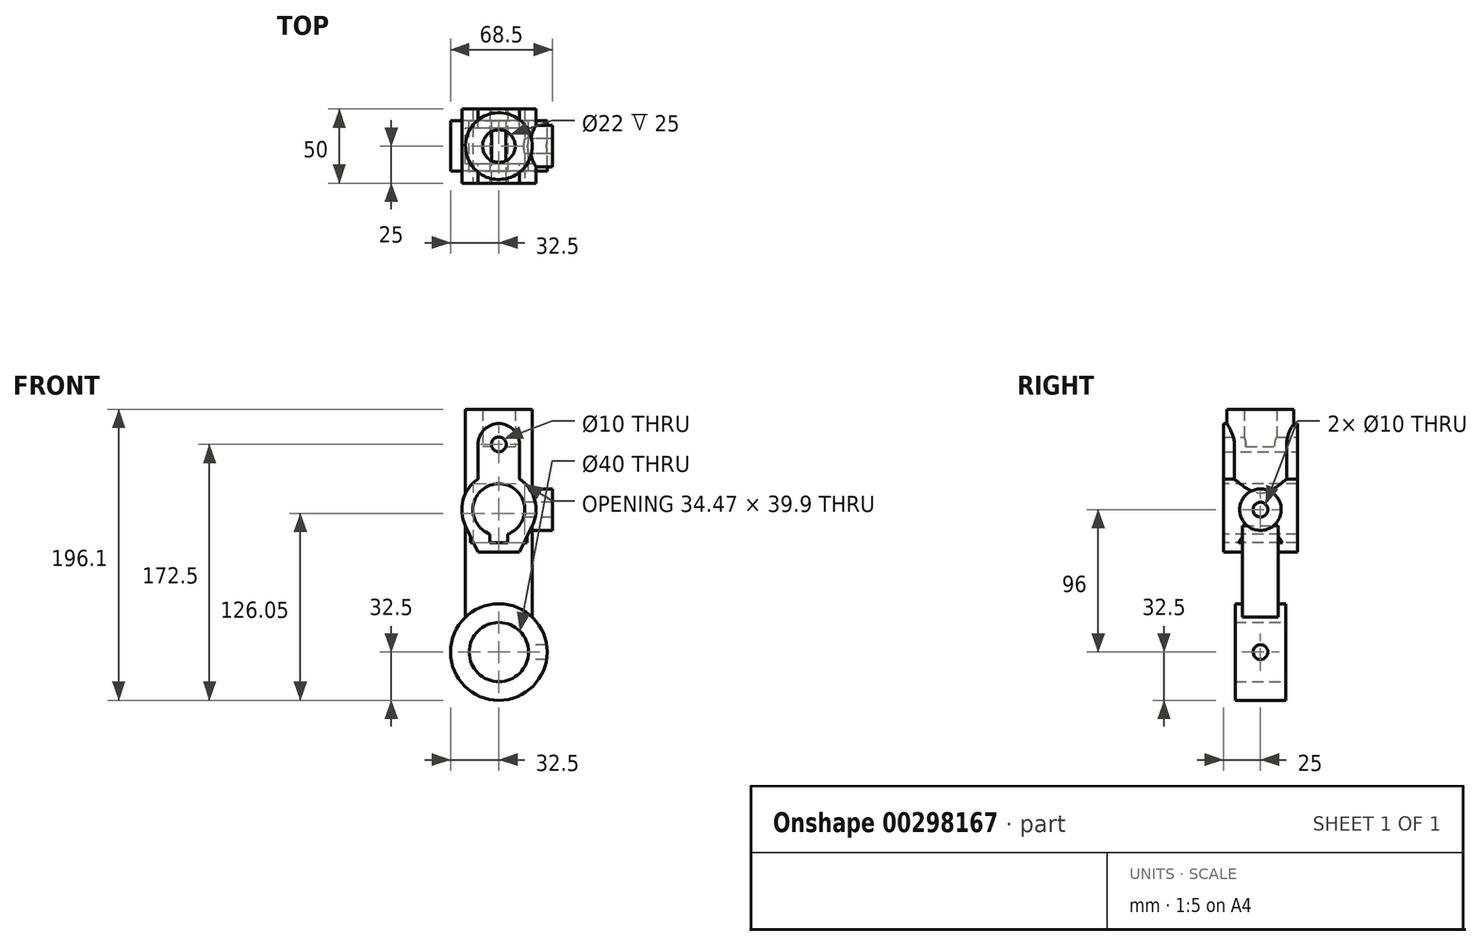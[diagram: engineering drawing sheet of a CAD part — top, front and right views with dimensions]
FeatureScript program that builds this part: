
annotation { "Feature Type Name" : "Feature", "Feature Type Description" : "" }
export const myFeature = defineFeature(function(context is Context, id is Id, definition is map)
    precondition{}
    {
        {
            var Q0;
            Q0=qCreatedBy(makeId("Front.planeOp"),FACE);
            var sketch = newSketch(context, id + "F0", { "sketchPlane" : qUnion([Q0])});
            skCircle(sketch, "E0", {"center": v(0, 0) * mm, "radius": 20 * mm});
            skCircle(sketch, "E1", {"center": v(0, 0) * mm, "radius": 32.5 * mm});
            skSolve(sketch);
        }
        {
            var Q0;
            Q0 = qSketchRegion(id + "F0", true);
            extrude(context, id + "F1", {"entities" : qUnion([Q0]), "endBound" : BoundingType.SYMMETRIC, "depth" : 34 * mm});
        }
        {
            var Q0;
            Q0=qCreatedBy(makeId("Right.planeOp"),FACE);
            var sketch = newSketch(context, id + "F2", { "sketchPlane" : qUnion([Q0])});
            skCircle(sketch, "E2", {"center": v(0, 0) * mm, "radius": 5 * mm});
            skSolve(sketch);
        }
        {
            var Q0;
            Q0 = qSketchRegion(id + "F2", true);
            extrude(context, id + "F3", {"entities" : qUnion([Q0]), "operationType" : NewBodyOperationType.REMOVE, "depth" : 100 * mm});
        }
        {
            var Q0;
            Q0=qCreatedBy(makeId("Front.planeOp"),FACE);
            var sketch = newSketch(context, id + "F4", { "sketchPlane" : qUnion([Q0])});
            skLineSegment(sketch, "E3.bottom", {"start": v(-22.5, 0) * mm, "end": v(22.5, 0) * mm});
            skLineSegment(sketch, "E3.top", {"start": v(-22.5, 96) * mm, "end": v(22.5, 96) * mm});
            skLineSegment(sketch, "E3.left", {"start": v(-22.5, 0) * mm, "end": v(-22.5, 96) * mm});
            skLineSegment(sketch, "E3.right", {"start": v(22.5, 0) * mm, "end": v(22.5, 96) * mm});
            skSolve(sketch);
        }
        {
            var Q0;
            Q0 = qSketchRegion(id + "F4", true);
            var Q1;
            Q1=makeQuery(id+"F1.opExtrude","SWEPT_FACE",FACE,{"disambiguationData":[OSD([sQuery(id+"F0.wireOp",EDGE,"E1")])]});
            var Q2;
            Q2=makeQuery(id+"F1.opExtrude","SWEPT_BODY",BODY,{"disambiguationData":[OSD([sQuery(id+"F0.wireOp",EDGE,"E0"),sQuery(id+"F0.wireOp",EDGE,"E1")])]});
            extrude(context, id + "F5", {"entities" : qUnion([Q0]), "operationType" : NewBodyOperationType.ADD, "endBound" : BoundingType.SYMMETRIC, "oppositeDirection" : true, "endBoundEntityFace" : qUnion([Q1]), "endBoundEntityBody" : qUnion([Q2]), "depth" : 24 * mm});
        }
        {
            var Q0;
            Q0=makeQuery(id+"F5.boolean.opBoolean","SPLIT",FACE,{"disambiguationData":[TD([makeQuery(id+"F3.boolean.opBoolean","COPY",FACE,{"derivedFrom":makeQuery(id+"F3.opExtrude","SWEPT_FACE",FACE,{"disambiguationData":[OSD([sQuery(id+"F2.wireOp",EDGE,"E2")])]})})])],"derivedFrom":makeQuery(id+"F5.opExtrude","SWEPT_FACE",FACE,{"disambiguationData":[OSD([sQuery(id+"F4.wireOp",EDGE,"E3.right")])]})});
            extrude(context, id + "F6", {"entities" : qUnion([Q0]), "operationType" : NewBodyOperationType.REMOVE, "oppositeDirection" : true, "depth" : 25 * mm});
        }
        {
            var Q0;
            {var subQ0=sQuery(id+"F4.wireOp",EDGE,"E3.bottom");Q0=makeQuery(id+"F5.boolean.opBoolean","SPLIT",FACE,{"disambiguationData":[TD([makeQuery(id+"F1.opExtrude","SWEPT_FACE",FACE,{"disambiguationData":[OSD([sQuery(id+"F0.wireOp",EDGE,"E0")])]})])],"derivedFrom":makeQuery(id+"F5.opExtrude","CAP_FACE",FACE,{"disambiguationData":[OSD([subQ0,sQuery(id+"F4.wireOp",EDGE,"E3.top"),sQuery(id+"F4.wireOp",EDGE,"E3.left"),sQuery(id+"F4.wireOp",EDGE,"E3.right")])],"isStart":true})});}
            extrude(context, id + "F7", {"entities" : qUnion([Q0]), "operationType" : NewBodyOperationType.REMOVE, "oppositeDirection" : true, "depth" : 25 * mm});
        }
        {
            var Q0;
            Q0=qCreatedBy(makeId("Front.planeOp"),FACE);
            var sketch = newSketch(context, id + "F8", { "sketchPlane" : qUnion([Q0])});
            skArc(sketch, "E4", {"start": v(6, 79.56) * mm, "mid": v(0, 113.5) * mm, "end": v(-6, 79.56) * mm});
            skLineSegment(sketch, "E5.bottom", {"start": v(6, 73.6) * mm, "end": v(-6, 73.6) * mm});
            skLineSegment(sketch, "E5.left", {"start": v(6, 73.6) * mm, "end": v(6, 79.56) * mm});
            skLineSegment(sketch, "E5.right", {"start": v(-6, 73.6) * mm, "end": v(-6, 79.56) * mm});
            skPoint(sketch, "E5.middle", {"position": v(0, 78.5) * mm});
            skPoint(sketch, "E6.orphan", {"position": v(6, 83.4) * mm});
            skPoint(sketch, "E7.orphan", {"position": v(-6, 83.4) * mm});
            skSolve(sketch);
        }
        {
            var Q0;
            Q0=qCreatedBy(makeId("Front.planeOp"),FACE);
            var sketch = newSketch(context, id + "F9", { "sketchPlane" : qUnion([Q0])});
            skArc(sketch, "E8", {"start": v(-14, 116.71) * mm, "mid": v(-24.14, 102.5) * mm, "end": v(-22.5, 85.1) * mm});
            skCircle(sketch, "E9", {"center": v(0, 140) * mm, "radius": 5 * mm});
            skArc(sketch, "E10", {"start": v(14, 140) * mm, "mid": v(0, 154) * mm, "end": v(-14, 140) * mm});
            skLineSegment(sketch, "E11", {"start": v(-14, 140) * mm, "end": v(-14, 116.71) * mm});
            skLineSegment(sketch, "E12", {"start": v(14, 140) * mm, "end": v(14, 116.71) * mm});
            skLineSegment(sketch, "E13", {"start": v(-22.5, 85.1) * mm, "end": v(-14, 67.55) * mm});
            skLineSegment(sketch, "E14", {"start": v(-14, 67.55) * mm, "end": v(14, 67.55) * mm});
            skLineSegment(sketch, "E15", {"start": v(14, 67.55) * mm, "end": v(22.5, 85.1) * mm});
            skArc(sketch, "E16.trimOffspring", {"start": v(22.5, 85.1) * mm, "mid": v(24.14, 102.5) * mm, "end": v(14, 116.71) * mm});
            skSolve(sketch);
        }
        {
            var Q0;
            Q0 = qSketchRegion(id + "F9", true);
            extrude(context, id + "F10", {"entities" : qUnion([Q0]), "operationType" : NewBodyOperationType.ADD, "endBound" : BoundingType.SYMMETRIC, "depth" : 50 * mm});
        }
        {
            var Q0;
            Q0 = qSketchRegion(id + "F8", true);
            extrude(context, id + "F11", {"entities" : qUnion([Q0]), "operationType" : NewBodyOperationType.REMOVE, "endBound" : BoundingType.SYMMETRIC, "oppositeDirection" : true, "depth" : 50 * mm});
        }
        {
            var Q0;
            Q0=qCreatedBy(makeId("Right.planeOp"),FACE);
            var sketch = newSketch(context, id + "F12", { "sketchPlane" : qUnion([Q0])});
            skCircle(sketch, "E17", {"center": v(0, 96) * mm, "radius": 5 * mm});
            skCircle(sketch, "E18", {"center": v(0, 96) * mm, "radius": 14 * mm});
            skSolve(sketch);
        }
        {
            var Q0;
            Q0 = qSketchRegion(id + "F12", true);
            extrude(context, id + "F13", {"entities" : qUnion([Q0]), "operationType" : NewBodyOperationType.ADD, "depth" : 36 * mm});
        }
        {
            var Q0;
            Q0 = qSketchRegion(id + "F8", true);
            extrude(context, id + "F14", {"entities" : qUnion([Q0]), "operationType" : NewBodyOperationType.REMOVE, "endBound" : BoundingType.SYMMETRIC, "oppositeDirection" : true, "depth" : 50 * mm});
        }
        {
            var Q0;
            Q0=makeQuery(id+"F11.boolean.opBoolean","COPY",FACE,{"derivedFrom":makeQuery(id+"F11.opExtrude","SWEPT_FACE",FACE,{"disambiguationData":[OSD([sQuery(id+"F8.wireOp",EDGE,"E5.bottom")])]})});
            var sketch = newSketch(context, id + "F15", { "sketchPlane" : qUnion([Q0])});
            skCircle(sketch, "E19", {"center": v(0, 0) * mm, "radius": 11 * mm});
            skCircle(sketch, "E20", {"center": v(0, 0) * mm, "radius": 22.5 * mm});
            skSolve(sketch);
        }
        {
            var Q0;
            Q0 = qSketchRegion(id + "F15", true);
            extrude(context, id + "F16", {"entities" : qUnion([Q0]), "operationType" : NewBodyOperationType.ADD, "depth" : 90 * mm});
        }
        {
            var Q0;
            Q0 = qSketchRegion(id + "F8", true);
            extrude(context, id + "F17", {"entities" : qUnion([Q0]), "operationType" : NewBodyOperationType.REMOVE, "endBound" : BoundingType.SYMMETRIC, "depth" : 50 * mm});
        }
        {
            var Q0;
            Q0=makeQuery(id+"F16.opExtrude","CAP_FACE",FACE,{"disambiguationData":[OSD([sQuery(id+"F15.wireOp",EDGE,"E19"),sQuery(id+"F15.wireOp",EDGE,"E20")])],"isStart":false});
            var sketch = newSketch(context, id + "F18", { "sketchPlane" : qUnion([Q0])});
            skCircle(sketch, "E21", {"center": v(0, 0) * mm, "radius": 11 * mm});
            skSolve(sketch);
        }
        {
            var Q0;
            Q0 = qSketchRegion(id + "F18", true);
            extrude(context, id + "F19", {"entities" : qUnion([Q0]), "operationType" : NewBodyOperationType.REMOVE, "oppositeDirection" : true, "depth" : 25 * mm});
        }
        {
            var Q0;
            Q0=makeQuery(id+"F10.opExtrude","CAP_FACE",FACE,{"disambiguationData":[OSD([sQuery(id+"F9.wireOp",EDGE,"E8"),sQuery(id+"F9.wireOp",EDGE,"E9"),sQuery(id+"F9.wireOp",EDGE,"E10"),sQuery(id+"F9.wireOp",EDGE,"E11"),sQuery(id+"F9.wireOp",EDGE,"E12"),sQuery(id+"F9.wireOp",EDGE,"E13"),sQuery(id+"F9.wireOp",EDGE,"E14"),sQuery(id+"F9.wireOp",EDGE,"E15"),sQuery(id+"F9.wireOp",EDGE,"E16.trimOffspring")])],"isStart":false});
            var sketch = newSketch(context, id + "F20", { "sketchPlane" : qUnion([Q0])});
            skCircle(sketch, "E22", {"center": v(0, 140) * mm, "radius": 5 * mm});
            skSolve(sketch);
        }
        {
            var Q0;
            Q0 = qSketchRegion(id + "F20", true);
            extrude(context, id + "F21", {"entities" : qUnion([Q0]), "operationType" : NewBodyOperationType.REMOVE, "oppositeDirection" : true, "depth" : 50 * mm});
        }
        {
            var Q0;
            Q0=qCreatedBy(makeId("Right.planeOp"),FACE);
            var sketch = newSketch(context, id + "F22", { "sketchPlane" : qUnion([Q0])});
            skCircle(sketch, "E23", {"center": v(0, 96) * mm, "radius": 5 * mm});
            skSolve(sketch);
        }
        {
            var Q0;
            Q0 = qSketchRegion(id + "F22", true);
            extrude(context, id + "F23", {"entities" : qUnion([Q0]), "operationType" : NewBodyOperationType.REMOVE, "depth" : 50 * mm});
        }
    });
